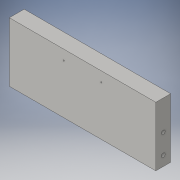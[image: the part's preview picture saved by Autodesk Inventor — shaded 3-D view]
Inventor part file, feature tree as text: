
AUTODESK INVENTOR PART (.ipt)
format: ipt  version: 2016 (Build 200138000, 138)  size: 635,392 bytes
history: native  units: in
note: dims shown in document units (in); Inventor stores cm internally (conversion verified against a paired STEP export)
features: sketch x7, extrude x4, hole x3
ambient origin geometry x8: Origin, YZ Plane, XZ Plane, XY Plane, X Axis, Y Axis, Z Axis, Center Point
bodies: Solid1 (feature_tree)
feature tree (14):
  extrude  "Extrusion1"  Depth=0.75in
  hole  "Hole1"  [1 undecoded]
  extrude  "Extrusion3"  Depth=1.0in
  hole  "Hole2"  [1 undecoded]
  extrude  "Extrusion4"  Depth=0.75in
  extrude  "Extrusion5"  Depth=0.2in TaperAngle=0.0deg
  hole  "Hole3"  [1 undecoded]
  sketch  "Sketch1"  dims[d0=7.4in d1=0.75in]
  sketch  "Sketch2"  dims[d2=3.0in d3=0.0in d4=0.0in]
  sketch  "Sketch4"  dims[d5=0.375in d6=1.0in]
  sketch  "Sketch5"  dims[d7=0.5in]
  sketch  "Sketch6"  dims[d8=0.1935in d9=0.75in d10=0.375in d11=0.25in d12=0.5635in d13=1.0in d14=0.8108in d21=0.75in]
  sketch  "Sketch7"  dims[d22=0.5in d23=0.75in]
  sketch  "Sketch8"  dims[d24=0.75in d25=0.2in d26=0.0in d27=1.9in d28=2.75in d30=0.5in d31=0.5in d32=2.75in d33=0.06in d34=0.75in d35=0.375in d36=0.25in d37=0.5635in d38=1.0in d39=0.8108in d40=0.1in d41=0.0in d42=0.12in d43=0.0in d44=2.0in d45=1.75in d46=0.375in d47=0.375in d48=0.25in d49=2.0in d50=0.1935in d51=0.75in d52=0.375in d53=0.25in d54=0.5635in d55=1.25in d56=0.8108in]
note: 3 required parameter values undecoded (feature->parameter linkage not recoverable at this tier; creation-order binding heuristic only, values carry confidence <= 0.55)
